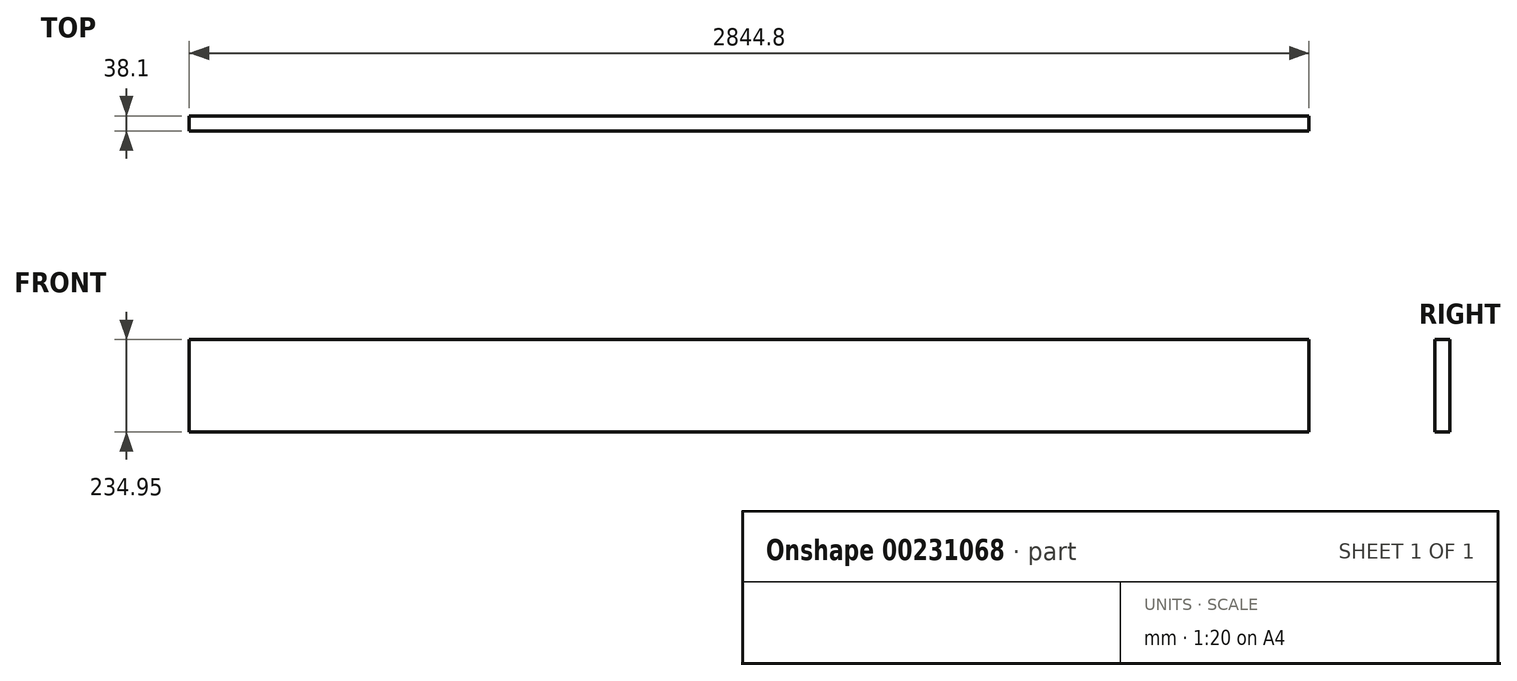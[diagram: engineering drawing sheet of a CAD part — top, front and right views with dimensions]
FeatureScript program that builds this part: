
annotation { "Feature Type Name" : "Feature", "Feature Type Description" : "" }
export const myFeature = defineFeature(function(context is Context, id is Id, definition is map)
    precondition{}
    {
        {
            var Q0;
            Q0=qCreatedBy(makeId("Right.planeOp"),FACE);
            var sketch = newSketch(context, id + "F0", { "sketchPlane" : qUnion([Q0])});
            skLineSegment(sketch, "E0.bottom", {"start": v(0, 0) * mm, "end": v(38.1, 0) * mm});
            skLineSegment(sketch, "E0.top", {"start": v(0, 234.95) * mm, "end": v(38.1, 234.95) * mm});
            skLineSegment(sketch, "E0.left", {"start": v(0, 0) * mm, "end": v(0, 234.95) * mm});
            skLineSegment(sketch, "E0.right", {"start": v(38.1, 0) * mm, "end": v(38.1, 234.95) * mm});
            skSolve(sketch);
        }
        {
            var Q0;
            Q0 = qSketchRegion(id + "F0", true);
            extrude(context, id + "F1", {"entities" : qUnion([Q0]), "depth" : 2844.8 * mm});
        }
    });
